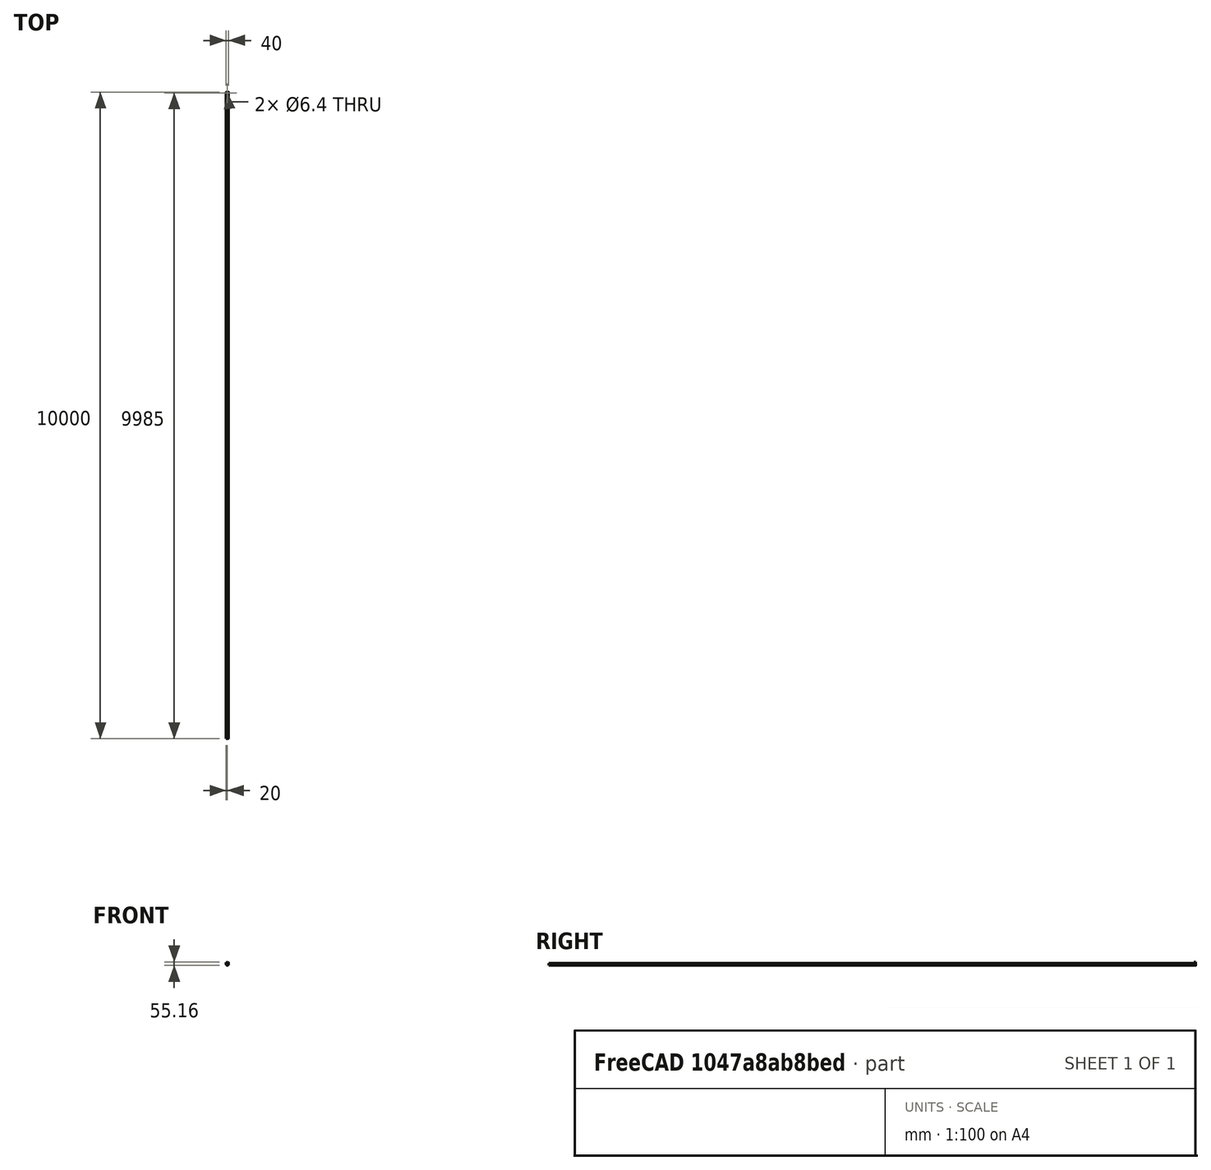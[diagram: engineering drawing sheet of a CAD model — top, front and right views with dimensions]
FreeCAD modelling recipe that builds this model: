
FCSTD DOCUMENT  (FreeCAD 0.16R)
Label: 30mmMount
License: All rights reserved
LicenseURL: http://en.wikipedia.org/wiki/All_rights_reserved
objects: Sketcher::SketchObject×6, PartDesign::Pocket×5, PartDesign::Fillet×3, PartDesign::Chamfer×2, PartDesign::Pad×1, Mesh::Feature×1
note: 23 computed .brp shape members not serialized (recipe doc carries the construction recipe); baked Part::Feature solids carry a one-line shape summary decoded from their .brp

FEATURE [Sketcher::SketchObject] Sketch
  sketch-geometry (4):
    g0: LineSegment StartX=-20 StartY=15 StartZ=0 EndX=20 EndY=15 EndZ=0
    g1: LineSegment StartX=20 StartY=15 StartZ=0 EndX=20 EndY=-15 EndZ=0
    g2: LineSegment StartX=20 StartY=-15 StartZ=0 EndX=-20 EndY=-15 EndZ=0
    g3: LineSegment StartX=-20 StartY=-15 StartZ=0 EndX=-20 EndY=15 EndZ=0
  constraints (11):
    c: Coincident(g0,g1)
    c: Coincident(g1,g2)
    c: Coincident(g2,g3)
    c: Coincident(g3,g0)
    c: Horizontal(g0)
    c: Horizontal(g2)
    c: Vertical(g1)
    c: Vertical(g3)
    c: Symmetric(g1,g0,g-1)
    c: Distance(g0) = 40
    c: Distance(g1) = 30
FEATURE [PartDesign::Pad] Pad
  Length = 30
  Length2 = 100
  Sketch = -> Sketch
  Type = 0
FEATURE [Sketcher::SketchObject] Sketch001
  Placement = pos=(0,15,0) rot=(0,0.707107,0.707107;3.14159rad)
  Support = -> Pad [Face1]
  sketch-geometry (1):
    g0: Circle CenterX=0 CenterY=0 CenterZ=0 NormalX=0 NormalY=0 NormalZ=1 Radius=17
  constraints (2):
    c: Coincident(g0,g-1)
    c: Radius(g0) = 17
FEATURE [PartDesign::Pocket] Pocket
  Length = 5
  Sketch = -> Sketch001
  Type = 1
FEATURE [Sketcher::SketchObject] Sketch002
  Placement = pos=(0,0,0) rot=(1,0,0;3.14159rad)
  Support = -> Pocket [Face2]
  sketch-geometry (7):
    g0: LineSegment StartX=5.75396 StartY=-0.474666 StartZ=0 EndX=3.28805 EndY=4.74574 EndZ=0
    g1: LineSegment StartX=3.28805 StartY=4.74574 StartZ=0 EndX=-2.46591 EndY=5.22041 EndZ=0
    g2: LineSegment StartX=-2.46591 StartY=5.22041 StartZ=0 EndX=-5.75396 EndY=0.474666 EndZ=0
    g3: LineSegment StartX=-5.75396 StartY=0.474666 StartZ=0 EndX=-3.28805 EndY=-4.74574 EndZ=0
    g4: LineSegment StartX=-3.28805 StartY=-4.74574 StartZ=0 EndX=2.46591 EndY=-5.22041 EndZ=0
    g5: LineSegment StartX=2.46591 StartY=-5.22041 StartZ=0 EndX=5.75396 EndY=-0.474666 EndZ=0
    g6: Circle [constr] CenterX=0 CenterY=0 CenterZ=0 NormalX=0 NormalY=0 NormalZ=1 Radius=5.7735
  constraints (16):
    c: Coincident(g0,g1)
    c: Coincident(g1,g2)
    c: Coincident(g2,g3)
    c: Coincident(g3,g4)
    c: Coincident(g4,g5)
    c: Coincident(g5,g0)
    c: Equal(g0, g1-g5) x5
    c: PointOnObject(g0,g6)
    c: PointOnObject(g1,g6)
    c: PointOnObject(g2,g6)
    c: PointOnObject(g3,g6)
    c: PointOnObject(g4,g6)
    c: PointOnObject(g5,g6)
    c: Coincident(g6,g-1)
    c: Distance(g0,g2) = 10
    c: DistanceY(g0) = 4.74574
FEATURE [PartDesign::Pocket] Pocket001
  Length = 21
  Sketch = -> Sketch002
  Type = 0
FEATURE [Sketcher::SketchObject] Sketch003
  Placement = pos=(0,0,30) rot=(0,0,1;0rad)
  Support = -> Pocket001 [Face6]
  sketch-geometry (1):
    g0: Circle CenterX=0 CenterY=0 CenterZ=0 NormalX=0 NormalY=0 NormalZ=1 Radius=3.2
  constraints (2):
    c: Radius(g0) = 3.2
    c: Coincident(g0,g-1)
FEATURE [PartDesign::Pocket] Pocket002
  Length = 5
  Sketch = -> Sketch003
  Type = 1
FEATURE [PartDesign::Fillet] Fillet
  Base = -> Pocket002 [Edge4,Edge6,Edge25,Edge20]
  Radius = 2
FEATURE [PartDesign::Chamfer] Chamfer
  Base = -> Fillet [Edge4,Edge23,Edge27,Edge24]
  Size = 1
FEATURE [Sketcher::SketchObject] Sketch004
  Placement = pos=(20,0,0) rot=(0.57735,0.57735,0.57735;2.0944rad)
  Support = -> Chamfer [Face14]
  sketch-geometry (8):
    g0: LineSegment StartX=-10.2729 StartY=37.2772 StartZ=0 EndX=-5.27291 EndY=37.2772 EndZ=0
    g1: LineSegment StartX=-5.27291 StartY=37.2772 StartZ=0 EndX=-5.27291 EndY=-8.94132 EndZ=0
    g2: LineSegment StartX=-5.27291 StartY=-8.94132 StartZ=0 EndX=-10.2729 EndY=-8.94132 EndZ=0
    g3: LineSegment StartX=-10.2729 StartY=-8.94132 StartZ=0 EndX=-10.2729 EndY=37.2772 EndZ=0
    g4: LineSegment StartX=5.27291 StartY=38.1563 StartZ=0 EndX=10.2729 EndY=38.1563 EndZ=0
    g5: LineSegment StartX=10.2729 StartY=38.1563 StartZ=0 EndX=10.2729 EndY=-8.94132 EndZ=0
    g6: LineSegment StartX=10.2729 StartY=-8.94132 StartZ=0 EndX=5.27291 EndY=-8.94132 EndZ=0
    g7: LineSegment StartX=5.27291 StartY=-8.94132 StartZ=0 EndX=5.27291 EndY=38.1563 EndZ=0
  constraints (19):
    c: Coincident(g0,g1)
    c: Coincident(g1,g2)
    c: Coincident(g2,g3)
    c: Coincident(g3,g0)
    c: Horizontal(g0)
    c: Horizontal(g2)
    c: Vertical(g1)
    c: Vertical(g3)
    c: Coincident(g4,g5)
    c: Coincident(g5,g6)
    c: Coincident(g6,g7)
    c: Coincident(g7,g4)
    c: Horizontal(g4)
    c: Horizontal(g6)
    c: Vertical(g5)
    c: Vertical(g7)
    c: Distance(g0) = 5
    c: Distance(g4) = 5
    c: Symmetric(g6,g1,g-2)
FEATURE [PartDesign::Pocket] Pocket003
  Length = 1
  Sketch = -> Sketch004
  Type = 0
FEATURE [Sketcher::SketchObject] Sketch005
  Placement = pos=(-20,0,0) rot=(0.57735,-0.57735,-0.57735;2.0944rad)
  Support = -> Pocket003 [Face9]
  sketch-geometry (8):
    g0: LineSegment StartX=-10.2729 StartY=37.2772 StartZ=0 EndX=-5.27291 EndY=37.2772 EndZ=0
    g1: LineSegment StartX=-5.27291 StartY=37.2772 StartZ=0 EndX=-5.27291 EndY=-8.94132 EndZ=0
    g2: LineSegment StartX=-5.27291 StartY=-8.94132 StartZ=0 EndX=-10.2729 EndY=-8.94132 EndZ=0
    g3: LineSegment StartX=-10.2729 StartY=-8.94132 StartZ=0 EndX=-10.2729 EndY=37.2772 EndZ=0
    g4: LineSegment StartX=5.27291 StartY=38.1563 StartZ=0 EndX=10.2729 EndY=38.1563 EndZ=0
    g5: LineSegment StartX=10.2729 StartY=38.1563 StartZ=0 EndX=10.2729 EndY=-8.94132 EndZ=0
    g6: LineSegment StartX=10.2729 StartY=-8.94132 StartZ=0 EndX=5.27291 EndY=-8.94132 EndZ=0
    g7: LineSegment StartX=5.27291 StartY=-8.94132 StartZ=0 EndX=5.27291 EndY=38.1563 EndZ=0
  constraints (19):
    c: Coincident(g0,g1)
    c: Coincident(g1,g2)
    c: Coincident(g2,g3)
    c: Coincident(g3,g0)
    c: Horizontal(g0)
    c: Horizontal(g2)
    c: Vertical(g1)
    c: Vertical(g3)
    c: Coincident(g4,g5)
    c: Coincident(g5,g6)
    c: Coincident(g6,g7)
    c: Coincident(g7,g4)
    c: Horizontal(g4)
    c: Horizontal(g6)
    c: Vertical(g5)
    c: Vertical(g7)
    c: Distance(g0) = 5
    c: Distance(g4) = 5
    c: Symmetric(g6,g1,g-2)
FEATURE [PartDesign::Pocket] Pocket004
  Length = 1
  Sketch = -> Sketch005
  Type = 0
FEATURE [PartDesign::Chamfer] Chamfer001
  Base = -> Pocket004 [Edge54,Edge58,Edge55,Edge59]
  Size = 4
FEATURE [PartDesign::Fillet] Fillet001
  Base = -> Chamfer001 [Edge49,Edge38,Edge29,Edge41,Edge70,Edge81,Edge89,Edge78]
  Radius = 0.5
FEATURE [PartDesign::Fillet] Fillet002
  Base = -> Fillet001 [Edge66,Edge69]
  Radius = 0.5
FEATURE [Mesh::Feature] Mesh  label="Fillet002 (Meshed)"
